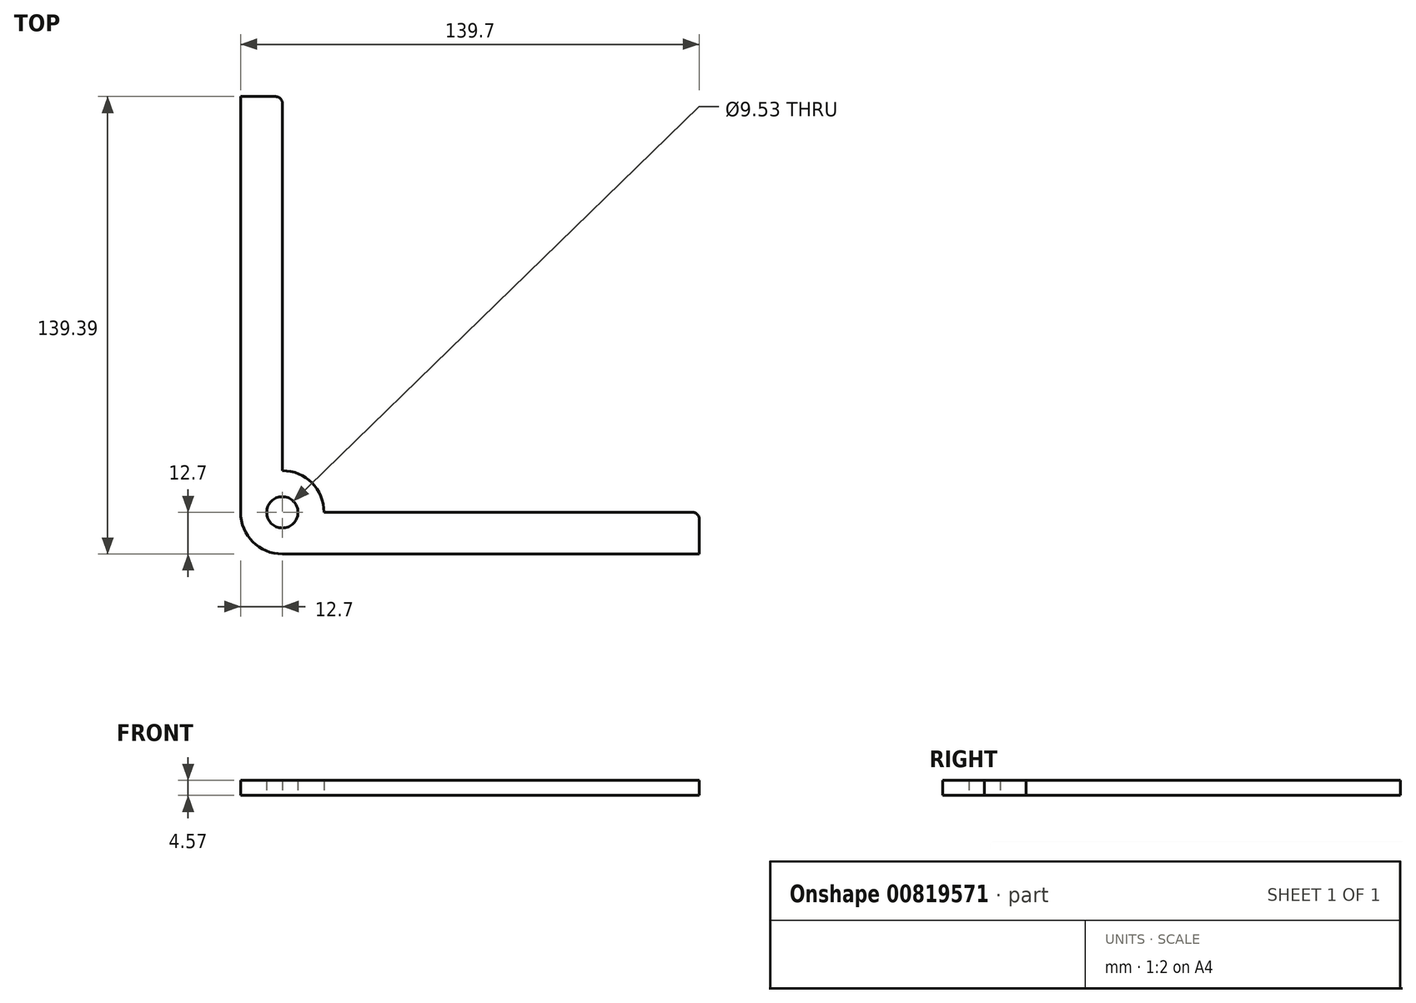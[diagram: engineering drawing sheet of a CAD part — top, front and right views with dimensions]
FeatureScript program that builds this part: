
annotation { "Feature Type Name" : "Feature", "Feature Type Description" : "" }
export const myFeature = defineFeature(function(context is Context, id is Id, definition is map)
    precondition{}
    {
        {
            var Q0;
            Q0=qCreatedBy(makeId("Top.planeOp"),FACE);
            var sketch = newSketch(context, id + "F0", { "sketchPlane" : qUnion([Q0])});
            skCircle(sketch, "E0", {"center": v(0, 0) * mm, "radius": 12.7 * mm});
            skCircle(sketch, "E1", {"center": v(0, 0) * mm, "radius": 4.76 * mm});
            skLineSegment(sketch, "E2", {"start": v(0, -12.7) * mm, "end": v(127, -12.7) * mm});
            skLineSegment(sketch, "E3", {"start": v(127, -12.7) * mm, "end": v(127, 0) * mm});
            skLineSegment(sketch, "E4", {"start": v(127, 0) * mm, "end": v(12.7, 0) * mm});
            skLineSegment(sketch, "E5", {"start": v(-12.7, 0) * mm, "end": v(-12.7, 127) * mm});
            skLineSegment(sketch, "E6", {"start": v(-12.7, 127) * mm, "end": v(-12.7, 126.7) * mm});
            skLineSegment(sketch, "E7", {"start": v(-12.7, 126.7) * mm, "end": v(0, 126.7) * mm});
            skLineSegment(sketch, "E8", {"start": v(0, 126.7) * mm, "end": v(0, 12.7) * mm});
            skSolve(sketch);
        }
        {
            var Q0;
            Q0 = qSketchRegion(id + "F0", true);
            extrude(context, id + "F1", {"entities" : qUnion([Q0]), "depth" : 4.57 * mm, "offsetDistance" : 25.4 * mm});
        }
        {
            var Q0;
            Q0=makeQuery(id+"F1.opExtrude","SWEPT_EDGE",EDGE,{"disambiguationData":[OSD([sQuery(id+"F0.wireOp",EDGE,"E7"),sQuery(id+"F0.wireOp",EDGE,"E8")])]});
            var Q1;
            Q1=makeQuery(id+"F1.opExtrude","SWEPT_EDGE",EDGE,{"disambiguationData":[OSD([sQuery(id+"F0.wireOp",EDGE,"E3"),sQuery(id+"F0.wireOp",EDGE,"E4")])]});
            fillet(context, id + "F2", {"entities" : qUnion([Q0, Q1]), "radius" : 2.03 * mm, "tangentPropagation" : true, "allowEdgeOverflow" : false});
        }
    });
